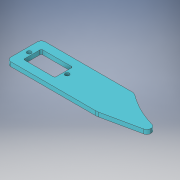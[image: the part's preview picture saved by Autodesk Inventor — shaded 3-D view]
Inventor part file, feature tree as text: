
AUTODESK INVENTOR PART (.ipt)
format: ipt  version: 2019.1 (Build 231200000, 200)  size: 145,920 bytes
history: native  units: in
note: dims shown in document units (in); Inventor stores cm internally (conversion verified against a paired STEP export)
features: extrude x1, sketch x1
ambient origin geometry x8: Origin, YZ Plane, XZ Plane, XY Plane, X Axis, Y Axis, Z Axis, Center Point
bodies: Solid1 (feature_tree)
feature tree (2):
  extrude  "Extrusion1"  Depth=0.1181in
  sketch  "Sketch1"  dims[d0=0.5118in d1=0.2362in d2=0.2362in d3=0.1181in d4=0.4921in d5=0.4921in d6=0.2362in d7=0.1181in d8=0.1181in d9=0.0394in d10=0.1181in d11=0.0394in d12=0.0394in d13=0.1969in d14=0.3937in d15=0.1181in d16=0.1181in d17=0.122in d18=0.0in]
